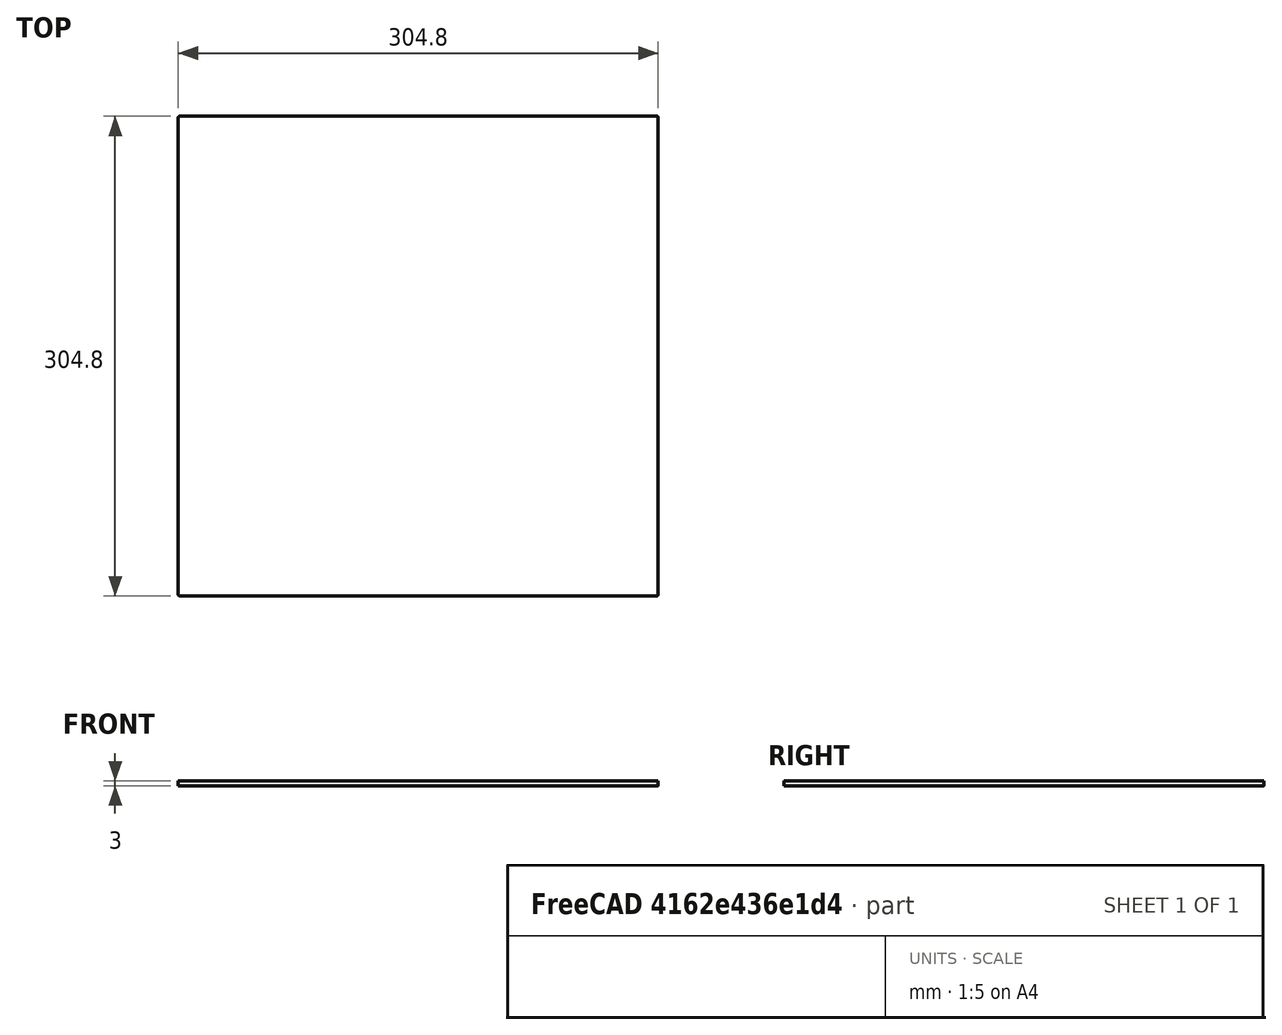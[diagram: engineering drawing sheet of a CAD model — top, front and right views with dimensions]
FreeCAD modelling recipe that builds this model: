
FCSTD DOCUMENT  (FreeCAD 0.20R29603 (Git))
Label: 12in_x_12in
License: All rights reserved
LicenseURL: http://en.wikipedia.org/wiki/All_rights_reserved
objects: Spreadsheet::Sheet×1, Sketcher::SketchObject×1, PartDesign::Pad×1, PartDesign::Body×1
note: 4 computed .brp shape members not serialized (recipe doc carries the construction recipe); baked Part::Feature solids carry a one-line shape summary decoded from their .brp

FEATURE [Spreadsheet::Sheet] Spreadsheet
  cells = A2=Length; B2(Length)==12in; A3=Width; B3(Width)==12in; A4=Thickness; B4(Thickness)==3mm; A5=FilletRadius; B5(FilletRadius)==1mm
FEATURE [Sketcher::SketchObject] Sketch
  FullyConstrained = true
  MapMode = 5
  Support = -> [XY_Plane]
  expr: Constraints[19] = Spreadsheet.FilletRadius
  expr: Constraints[21] = Spreadsheet.Length
  expr: Constraints[22] = Spreadsheet.Width
  sketch-geometry (10):
    g0: ArcOfCircle CenterX=-151.4 CenterY=151.4 CenterZ=0 NormalX=0 NormalY=0 NormalZ=1 AngleXU=0 Radius=1 StartAngle=1.5708 EndAngle=3.14159
    g1: LineSegment StartX=-151.4 StartY=152.4 StartZ=0 EndX=151.4 EndY=152.4 EndZ=0
    g2: ArcOfCircle CenterX=151.4 CenterY=151.4 CenterZ=0 NormalX=0 NormalY=0 NormalZ=1 AngleXU=0 Radius=1 StartAngle=1.8e-15 EndAngle=1.5708
    g3: LineSegment StartX=152.4 StartY=151.4 StartZ=0 EndX=152.4 EndY=-151.4 EndZ=0
    g4: ArcOfCircle CenterX=151.4 CenterY=-151.4 CenterZ=0 NormalX=0 NormalY=0 NormalZ=1 AngleXU=0 Radius=1 StartAngle=4.71239 EndAngle=6.28319
    g5: LineSegment StartX=151.4 StartY=-152.4 StartZ=0 EndX=-151.4 EndY=-152.4 EndZ=0
    g6: ArcOfCircle CenterX=-151.4 CenterY=-151.4 CenterZ=0 NormalX=0 NormalY=0 NormalZ=1 AngleXU=0 Radius=1 StartAngle=3.14159 EndAngle=4.71239
    g7: LineSegment StartX=-152.4 StartY=-151.4 StartZ=0 EndX=-152.4 EndY=151.4 EndZ=0
    g8: GeomPoint X=-152.4 Y=152.4 Z=0
    g9: GeomPoint X=152.4 Y=-152.4 Z=0
  constraints (23):
    c: Tangent(g0,g1) = 1.5708
    c: Tangent(g1,g2) = 1.5708
    c: Tangent(g2,g3) = 1.5708
    c: Tangent(g3,g4) = 1.5708
    c: Tangent(g4,g5) = 1.5708
    c: Tangent(g5,g6) = 1.5708
    c: Tangent(g6,g7) = 1.5708
    c: Tangent(g7,g0) = 1.5708
    c: Horizontal(g1)
    c: Horizontal(g5)
    c: Vertical(g3)
    c: Vertical(g7)
    c: Equal(g0,g2)
    c: Equal(g2,g4)
    c: Equal(g4,g6)
    c: PointOnObject(g8,g1)
    c: PointOnObject(g8,g7)
    c: PointOnObject(g9,g3)
    c: PointOnObject(g9,g5)
    c: Radius(g4) = 1
    c: Symmetric(g8,g9,g-1)
    c: DistanceX(g6,g3) = 304.8
    c: DistanceY(g4,g1) = 304.8
FEATURE [PartDesign::Pad] Pad
  Direction = (0,0,1)
  Length = 3
  Length2 = 10
  Profile = -> Sketch
  ReferenceAxis = -> Sketch [N_Axis]
  Type = 0
  expr: Length = Spreadsheet.Thickness
FEATURE [PartDesign::Body] Body
  Group = -> [Sketch,Pad]
  Origin = -> Origin
  Tip = -> Pad
